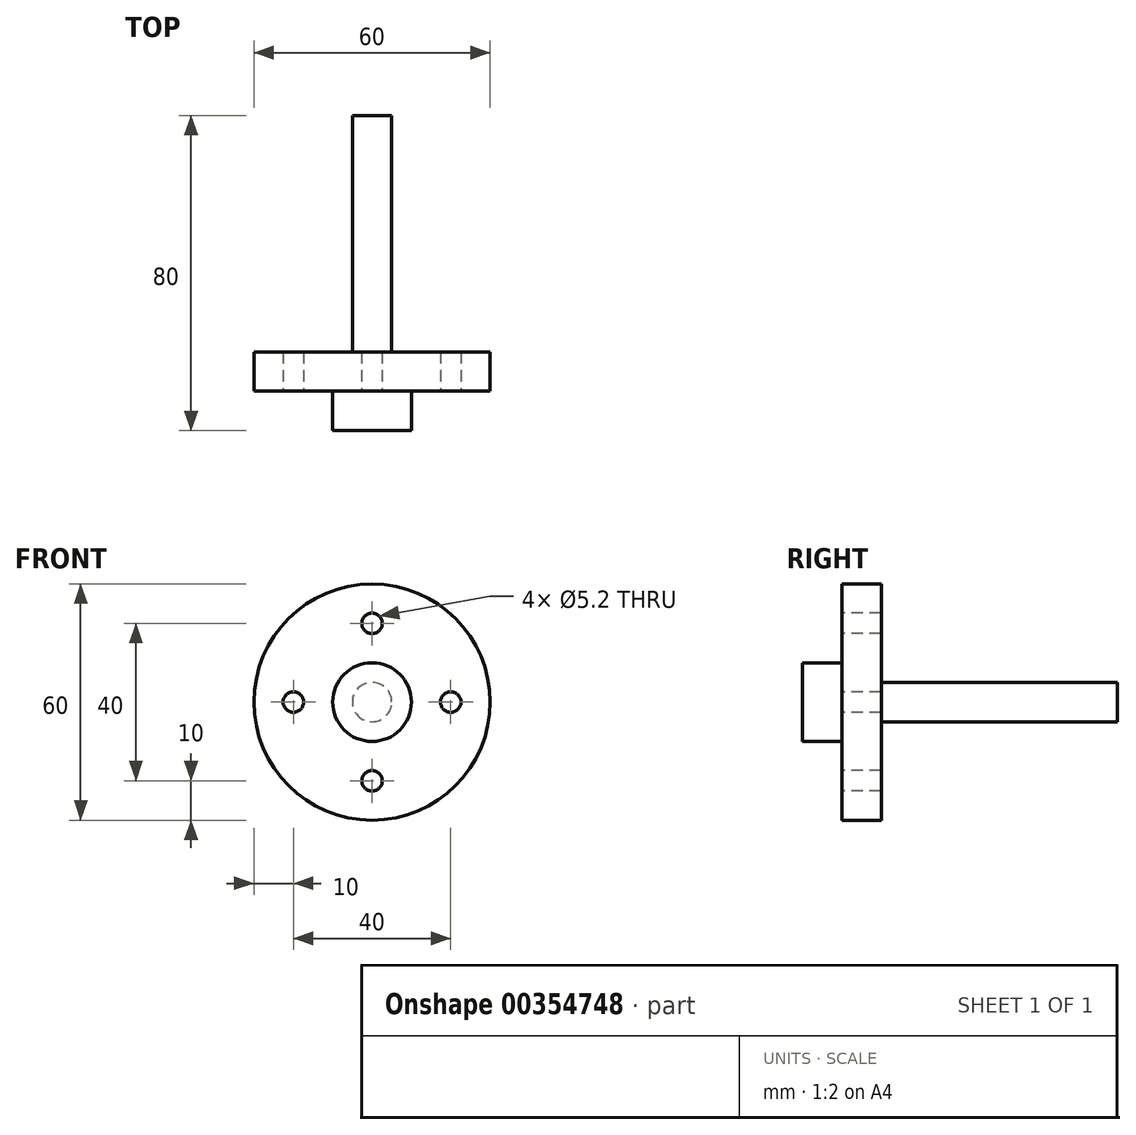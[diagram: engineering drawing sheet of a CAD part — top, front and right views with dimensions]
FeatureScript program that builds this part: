
annotation { "Feature Type Name" : "Feature", "Feature Type Description" : "" }
export const myFeature = defineFeature(function(context is Context, id is Id, definition is map)
    precondition{}
    {
        {
            var Q0;
            Q0=qCreatedBy(makeId("Front.planeOp"),FACE);
            var sketch = newSketch(context, id + "F0", { "sketchPlane" : qUnion([Q0])});
            skCircle(sketch, "E0", {"center": v(0, 0) * mm, "radius": 30 * mm});
            skSolve(sketch);
        }
        {
            var Q0;
            Q0 = qSketchRegion(id + "F0", true);
            extrude(context, id + "F1", {"entities" : qUnion([Q0]), "depth" : 10 * mm});
        }
        {
            var Q0;
            Q0=makeQuery(id+"F1.opExtrude","CAP_FACE",FACE,{"disambiguationData":[OSD([sQuery(id+"F0.wireOp",EDGE,"E0")])],"isStart":false});
            var sketch = newSketch(context, id + "F2", { "sketchPlane" : qUnion([Q0])});
            skPoint(sketch, "E1.middle", {"position": v(0, 0) * mm});
            skCircle(sketch, "E2", {"center": v(-20, 0) * mm, "radius": 2.6 * mm});
            skCircle(sketch, "E3", {"center": v(20, 0) * mm, "radius": 2.6 * mm});
            skCircle(sketch, "E4", {"center": v(0, 20) * mm, "radius": 2.6 * mm});
            skCircle(sketch, "E5", {"center": v(0, -20) * mm, "radius": 2.6 * mm});
            skSolve(sketch);
        }
        {
            var Q0;
            Q0=makeQuery(id+"F2.imprint","IMPRINT",FACE,{"disambiguationData":[TD([[makeQuery(id+"F2.imprint","IMPRINT",EDGE,{"derivedFrom":sQuery(id+"F2.wireOp",EDGE,"E2")}),1.0]])]});
            var Q1;
            Q1=makeQuery(id+"F2.imprint","IMPRINT",FACE,{"disambiguationData":[TD([[makeQuery(id+"F2.imprint","IMPRINT",EDGE,{"derivedFrom":sQuery(id+"F2.wireOp",EDGE,"E4")}),1.0]])]});
            var Q2;
            Q2=makeQuery(id+"F2.imprint","IMPRINT",FACE,{"disambiguationData":[TD([[makeQuery(id+"F2.imprint","IMPRINT",EDGE,{"derivedFrom":sQuery(id+"F2.wireOp",EDGE,"E3")}),1.0]])]});
            var Q3;
            Q3=makeQuery(id+"F2.imprint","IMPRINT",FACE,{"disambiguationData":[TD([[makeQuery(id+"F2.imprint","IMPRINT",EDGE,{"derivedFrom":sQuery(id+"F2.wireOp",EDGE,"E5")}),1.0]])]});
            var Q4;
            Q4=sQuery(id+"F2.wireOp",EDGE,"E4");
            var Q5;
            Q5=sQuery(id+"F2.wireOp",EDGE,"E2");
            var Q6;
            Q6=sQuery(id+"F2.wireOp",EDGE,"E5");
            var Q7;
            Q7=sQuery(id+"F2.wireOp",EDGE,"E3");
            extrude(context, id + "F3", {"entities" : qUnion([Q0, Q1, Q2, Q3]), "operationType" : NewBodyOperationType.REMOVE, "surfaceEntities" : qUnion([Q4, Q5, Q6, Q7]), "oppositeDirection" : true, "depth" : 25 * mm});
        }
        {
            var Q0;
            Q0=makeQuery(id+"F1.opExtrude","CAP_FACE",FACE,{"disambiguationData":[OSD([sQuery(id+"F0.wireOp",EDGE,"E0")])],"isStart":false});
            var sketch = newSketch(context, id + "F4", { "sketchPlane" : qUnion([Q0])});
            skCircle(sketch, "E6", {"center": v(0, 0) * mm, "radius": 10 * mm});
            skSolve(sketch);
        }
        {
            var Q0;
            Q0 = qSketchRegion(id + "F4", true);
            extrude(context, id + "F5", {"entities" : qUnion([Q0]), "operationType" : NewBodyOperationType.ADD, "depth" : 10 * mm});
        }
        {
            var Q0;
            Q0=makeQuery(id+"F1.opExtrude","CAP_FACE",FACE,{"disambiguationData":[OSD([sQuery(id+"F0.wireOp",EDGE,"E0")])],"isStart":true});
            var sketch = newSketch(context, id + "F6", { "sketchPlane" : qUnion([Q0])});
            skCircle(sketch, "E7", {"center": v(0, 0) * mm, "radius": 5 * mm});
            skSolve(sketch);
        }
        {
            var Q0;
            Q0 = qSketchRegion(id + "F6", true);
            extrude(context, id + "F7", {"entities" : qUnion([Q0]), "operationType" : NewBodyOperationType.ADD, "depth" : 60 * mm});
        }
    });
